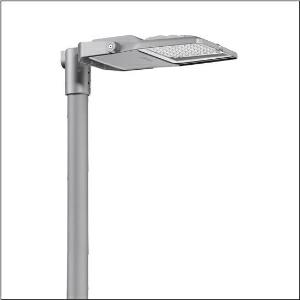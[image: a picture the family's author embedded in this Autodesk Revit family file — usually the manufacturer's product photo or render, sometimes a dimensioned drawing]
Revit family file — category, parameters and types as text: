
# Revit family: floodlight_fl_21_iq_mini___pl64_5xa7771d2e3a_d262
name_source: partatom
category: Lighting Fixtures
units: mm (PartAtom-declared; Revit-internal decimal feet)

## family parameters
Cut with Voids When Loaded = No
Host = Face
Light Source = No
Part Type = Normal
Room Calculation Point = No
Round Connector Dimension = Use Diameter
Shared = No

## types (1)
- --- (1 x LED, 17220 lm, 143 W, 3000K)
    Apparent Load = 143 VA
    CIE Flux Codes = 28 80 98 100 100
    Color Rendering = 70
    Color Temperature = 3000K
    Default Elevation = 1800 mm
    Description = Floodlight FL 21 iQ mini, floodlight, primary light control with lens, of PMMA, primary optical cover: protective disc, of toughened safety glass, transparent, light distribution: PL64, light emission: direct distribution, installation type: surface-mounted, lamps: LED, High Power LED, rated values: 17.220lm | 143W | 120,4lm/W (begin service life); end service life: 17.220lm | 151,6W; at 50% lumin. flux: 8.610lm | 60,6W | 142,1lm/W, colour temperature: 3000K, colour rendering: CRI > 70, light colour: 730, light setting 1 begin service life: 100% | 17.220lm | 143W | 120,4lm/W | 3.000K, light setting 1 end service life: 151,6W, further light settings possible, control: Auto-Match, Temp-Guard, Lumen-Switch, Night-Set, Smart-Wire, Light-Fading, Desk-Remote (wireless, voltage-free reading and setting of iQ features in the workshop via application-optimized NFC function/RFID function), optimised constant luminous flux control (CLO 2.0), pre-setting: linear dimming characteristic, with terminal, 6-pole, mains connection: 220..240V, AC, 50/60Hz, luminaire housing, of diecast aluminium, powder-coated, SITECO metallic grey (DB 702S), corrosivity category C5 mid according to DIN EN ISO 12944suitable for swimming poolschlorine-resistant, sealing non-destructively replaceable, please order mast flange separately, mast bracket, of steel, galvanised, powder-coated, SITECO metallic grey (DB 702S), protection rating (complete): IP66, insulation class (complete): insulation class II (safety insulation), certification: CE, ENEC, VDE, protection symbol: D, impact resistance: IK08, permissible operating ambient temperature: -40..+40°C, permissible operating ambient temperature for outdoor applications: -40..+50°C, standard: DIN EN 12944, LABS conformity tested according to VDMA 24364:2018-05, packaging unit: 1 piece

Light Distribution: PL64
    Height = 70 mm
    Lamp = 1 x LED
    Lamp Light Flux = 17220 lm
    Lamp Power = 143 W
    Lamp count = 1
    Length = 485 mm
    Luminous efficacy = 120 lm/W
    Manufacturer = Siteco
    ModVariant = No
    Model = 5XA7771D2E3A
    Mounting Place = Pole
    Mounting Type = Pole annexe
    Number of Poles = 1
    OnlyDefault = Yes
    Power Factor = 1
    Product Name = Floodlight FL 21 iQ mini | PL64
    Product group = floodlight | pylon annexe
    ProductGroupID = 6201
    Protection Class = Protection class II
    Protection Degree = IP 66
    RLX_Detail_Level = 1
    RLX_Emergency_Light_Flux = 0 lm
    RLX_Emergency_Type = 0
    RLX_Emergency_Type_DB = No
    RlxData = <blob elided: 101893 chars, md5=8f2a7316>
    Socket = socket
    Standby Power = 0 W
    System Light Flux = 17220 lm
    System Power = 143 W
    Type Comments = factory setting: luminous flux: 100 % | dim-lin: 254 | 730 mA
    Type Image = l_1007125.jpg
    URL = http://relux.com
    VarID = @adj_167101
    Voltage = 0 V
    Weight = 0.00 kg
    Width = 337 mm

## geometry (parser evidence)
native form markers: Blend x4, Sweep x11
no freeform markers — native parametric forms only
